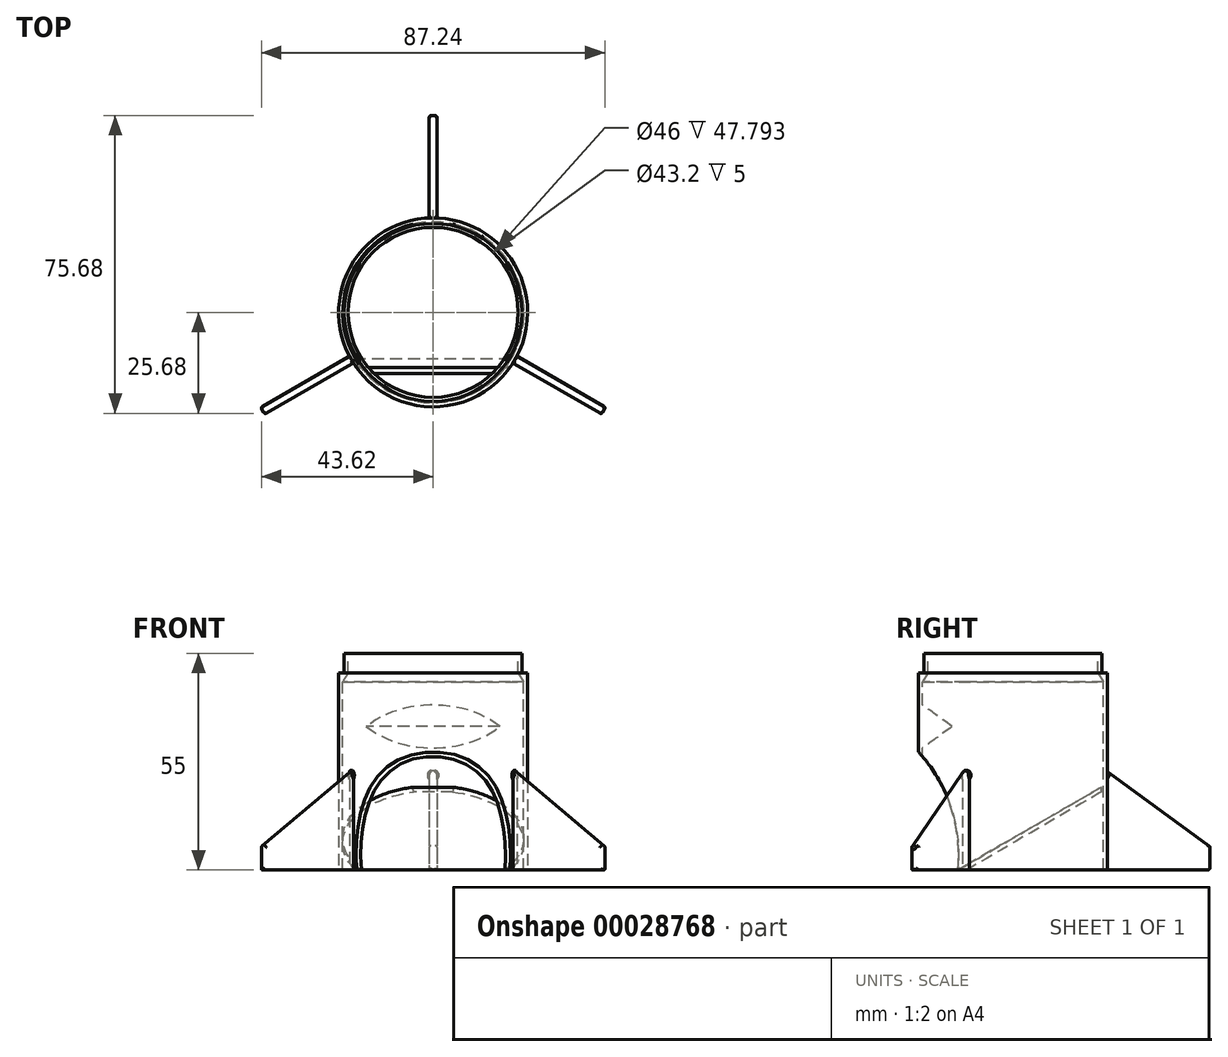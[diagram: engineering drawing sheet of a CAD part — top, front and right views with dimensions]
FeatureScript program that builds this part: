
annotation { "Feature Type Name" : "Feature", "Feature Type Description" : "" }
export const myFeature = defineFeature(function(context is Context, id is Id, definition is map)
    precondition{}
    {
        {
            var Q0;
            Q0=qCreatedBy(makeId("Top.planeOp"),FACE);
            var sketch = newSketch(context, id + "F0", { "sketchPlane" : qUnion([Q0])});
            skCircle(sketch, "E0", {"center": v(0, 0) * mm, "radius": 24 * mm});
            skSolve(sketch);
        }
        {
            var Q0;
            Q0=makeQuery(id+"F0.imprint","IMPRINT",FACE,{"disambiguationData":[TD([[makeQuery(id+"F0.imprint","IMPRINT",EDGE,{"derivedFrom":sQuery(id+"F0.wireOp",EDGE,"E0")}),1.0]])]});
            extrude(context, id + "F1", {"entities" : qUnion([Q0]), "depth" : 50 * mm});
        }
        {
            var Q0;
            Q0=makeQuery(id+"F1.opExtrude","CAP_FACE",FACE,{"disambiguationData":[OSD([sQuery(id+"F0.wireOp",EDGE,"E0")])],"isStart":false});
            var sketch = newSketch(context, id + "F2", { "sketchPlane" : qUnion([Q0])});
            skCircle(sketch, "E1", {"center": v(0, 0) * mm, "radius": 23 * mm});
            skSolve(sketch);
        }
        {
            var Q0;
            Q0=qSketchRegion(id+"F2",true);
            extrude(context, id + "F3", {"entities" : qUnion([Q0]), "operationType" : NewBodyOperationType.REMOVE, "endBound" : BoundingType.THROUGH_ALL, "oppositeDirection" : true, "depth" : 25 * mm});
        }
        {
            var Q0;
            Q0=qCreatedBy(makeId("Front.planeOp"),FACE);
            var sketch = newSketch(context, id + "F4", { "sketchPlane" : qUnion([Q0])});
            skLineSegment(sketch, "E2", {"start": v(0, 0) * mm, "end": v(0, 50) * mm});
            skLineSegment(sketch, "E3.0", {"start": v(-23.5, 50) * mm, "end": v(-23.5, 47) * mm});
            skLineSegment(sketch, "E4", {"start": v(-23.5, 50) * mm, "end": v(-22.6, 50) * mm});
            skLineSegment(sketch, "E5", {"start": v(-22.6, 50) * mm, "end": v(-22.6, 55) * mm});
            skLineSegment(sketch, "E6", {"start": v(-22.6, 55) * mm, "end": v(-21.6, 55) * mm});
            skLineSegment(sketch, "E7", {"start": v(-21.6, 55) * mm, "end": v(-21.6, 50) * mm});
            skLineSegment(sketch, "E8", {"start": v(-21.6, 50) * mm, "end": v(-23.5, 47) * mm});
            skLineSegment(sketch, "E9", {"start": v(-24, 50) * mm, "end": v(-23.5, 50) * mm});
            skSolve(sketch);
        }
        {
            var Q0;
            Q0=qSketchRegion(id+"F4",true);
            var Q1;
            Q1=makeQuery(id+"F3.boolean.opBoolean","COPY",FACE,{"derivedFrom":makeQuery(id+"F3.opExtrude","SWEPT_FACE",FACE,{"disambiguationData":[OSD([sQuery(id+"F2.wireOp",EDGE,"E1")])]})});
            revolve(context, id + "F5", {"operationType" : NewBodyOperationType.ADD, "entities" : qUnion([Q0]), "axis" : qUnion([Q1]), "revolveType" : RevolveType.FULL});
        }
        {
            var Q0;
            Q0=qCreatedBy(makeId("Top.planeOp"),FACE);
            var sketch = newSketch(context, id + "F6", { "sketchPlane" : qUnion([Q0])});
            skLineSegment(sketch, "E10", {"start": v(-1, 50) * mm, "end": v(-1, 23.5) * mm});
            skLineSegment(sketch, "E11", {"start": v(-1, 23.5) * mm, "end": v(1, 23.5) * mm});
            skLineSegment(sketch, "E12", {"start": v(1, 23.5) * mm, "end": v(1, 50) * mm});
            skLineSegment(sketch, "E13", {"start": v(-1, 50) * mm, "end": v(1, 50) * mm});
            skLineSegment(sketch, "E14.1.4", {"start": v(-20.85, -10.88) * mm, "end": v(-43.8, -24.13) * mm});
            skLineSegment(sketch, "E14.1.6", {"start": v(-42.8, -25.87) * mm, "end": v(-19.85, -12.62) * mm});
            skLineSegment(sketch, "E14.1.8", {"start": v(-19.85, -12.62) * mm, "end": v(-20.85, -10.88) * mm});
            skLineSegment(sketch, "E14.1.11", {"start": v(-42.8, -25.87) * mm, "end": v(-43.8, -24.13) * mm});
            skLineSegment(sketch, "E14.2.4", {"start": v(19.85, -12.62) * mm, "end": v(42.8, -25.87) * mm});
            skLineSegment(sketch, "E14.2.6", {"start": v(43.8, -24.13) * mm, "end": v(20.85, -10.88) * mm});
            skLineSegment(sketch, "E14.2.8", {"start": v(20.85, -10.88) * mm, "end": v(19.85, -12.62) * mm});
            skLineSegment(sketch, "E14.2.11", {"start": v(43.8, -24.13) * mm, "end": v(42.8, -25.87) * mm});
            skPoint(sketch, "E14.center", {"position": v(0, 0) * mm});
            skSolve(sketch);
        }
        {
            var Q0;
            Q0=qSketchRegion(id+"F6",true);
            extrude(context, id + "F7", {"entities" : qUnion([Q0]), "operationType" : NewBodyOperationType.ADD, "depth" : 25 * mm});
        }
        {
            var Q0;
            Q0=makeQuery(id+"F7.opExtrude","SWEPT_FACE",FACE,{"disambiguationData":[OSD([sQuery(id+"F6.wireOp",EDGE,"E14.1.6")])]});
            var sketch = newSketch(context, id + "F8", { "sketchPlane" : qUnion([Q0])});
            skLineSegment(sketch, "E15", {"start": v(-23.98, 25) * mm, "end": v(-50, 25) * mm});
            skLineSegment(sketch, "E16", {"start": v(-50, 25) * mm, "end": v(-50, 6) * mm});
            skLineSegment(sketch, "E17", {"start": v(-50, 6) * mm, "end": v(-23.98, 25) * mm});
            skSolve(sketch);
        }
        {
            var Q0;
            Q0=qSketchRegion(id+"F8",true);
            extrude(context, id + "F9", {"entities" : qUnion([Q0]), "operationType" : NewBodyOperationType.REMOVE, "oppositeDirection" : true, "depth" : 2 * mm});
        }
        {
            var Q0;
            Q0=makeQuery(id+"F7.opExtrude","SWEPT_FACE",FACE,{"disambiguationData":[OSD([sQuery(id+"F6.wireOp",EDGE,"E14.2.6")])]});
            var sketch = newSketch(context, id + "F10", { "sketchPlane" : qUnion([Q0])});
            skLineSegment(sketch, "E18", {"start": v(-23.98, 25) * mm, "end": v(-50, 25) * mm});
            skLineSegment(sketch, "E19", {"start": v(-50, 25) * mm, "end": v(-50, 6) * mm});
            skLineSegment(sketch, "E20", {"start": v(-50, 6) * mm, "end": v(-23.98, 25) * mm});
            skSolve(sketch);
        }
        {
            var Q0;
            Q0=qSketchRegion(id+"F10",true);
            extrude(context, id + "F11", {"entities" : qUnion([Q0]), "operationType" : NewBodyOperationType.REMOVE, "oppositeDirection" : true, "depth" : 2 * mm});
        }
        {
            var Q0;
            Q0=makeQuery(id+"F7.opExtrude","SWEPT_FACE",FACE,{"disambiguationData":[OSD([sQuery(id+"F6.wireOp",EDGE,"E10")])]});
            var sketch = newSketch(context, id + "F12", { "sketchPlane" : qUnion([Q0])});
            skLineSegment(sketch, "E21", {"start": v(-23.98, 25) * mm, "end": v(-50, 25) * mm});
            skLineSegment(sketch, "E22", {"start": v(-50, 25) * mm, "end": v(-50, 6) * mm});
            skLineSegment(sketch, "E23", {"start": v(-23.98, 25) * mm, "end": v(-50, 6) * mm});
            skSolve(sketch);
        }
        {
            var Q0;
            Q0=qSketchRegion(id+"F12",true);
            extrude(context, id + "F13", {"entities" : qUnion([Q0]), "operationType" : NewBodyOperationType.REMOVE, "oppositeDirection" : true, "depth" : 2 * mm});
        }
        {
            var Q0;
            Q0=makeQuery(id+"F13.boolean.opBoolean","COPY",FACE,{"derivedFrom":makeQuery(id+"F13.opExtrude","SWEPT_FACE",FACE,{"disambiguationData":[OSD([sQuery(id+"F12.wireOp",EDGE,"E23")])]})});
            var Q1;
            Q1=makeQuery(id+"F9.boolean.opBoolean","COPY",FACE,{"derivedFrom":makeQuery(id+"F9.opExtrude","SWEPT_FACE",FACE,{"disambiguationData":[OSD([sQuery(id+"F8.wireOp",EDGE,"E17")])]})});
            var Q2;
            Q2=makeQuery(id+"F11.boolean.opBoolean","COPY",FACE,{"derivedFrom":makeQuery(id+"F11.opExtrude","SWEPT_FACE",FACE,{"disambiguationData":[OSD([sQuery(id+"F10.wireOp",EDGE,"E20")])]})});
            fillet(context, id + "F14", {"entities" : qUnion([Q0, Q1, Q2]), "radius" : .5 * mm, "allowEdgeOverflow" : false});
        }
        {
            var Q0;
            Q0=makeQuery(id+"F7.opExtrude","SWEPT_FACE",FACE,{"disambiguationData":[OSD([sQuery(id+"F6.wireOp",EDGE,"E14.1.11")])]});
            var Q1;
            Q1=makeQuery(id+"F7.opExtrude","SWEPT_FACE",FACE,{"disambiguationData":[OSD([sQuery(id+"F6.wireOp",EDGE,"E14.2.11")])]});
            var Q2;
            Q2=makeQuery(id+"F7.opExtrude","SWEPT_FACE",FACE,{"disambiguationData":[OSD([sQuery(id+"F6.wireOp",EDGE,"E13")])]});
            fillet(context, id + "F15", {"entities" : qUnion([Q0, Q1, Q2]), "radius" : .5 * mm, "tangentPropagation" : true, "allowEdgeOverflow" : false});
        }
        {
            var Q0;
            Q0=qCreatedBy(makeId("Right.planeOp"),FACE);
            var sketch = newSketch(context, id + "F16", { "sketchPlane" : qUnion([Q0])});
            skLineSegment(sketch, "E24", {"start": v(-24, 0) * mm, "end": v(-24, 30) * mm});
            skArc(sketch, "E25", {"start": v(-14, 0) * mm, "mid": v(-15.84, 16.05) * mm, "end": v(-24, 30) * mm});
            skLineSegment(sketch, "E26", {"start": v(-24, 0) * mm, "end": v(-14, 0) * mm});
            skSolve(sketch);
        }
        {
            var Q0;
            Q0=qSketchRegion(id+"F16",true);
            extrude(context, id + "F17", {"entities" : qUnion([Q0]), "operationType" : NewBodyOperationType.REMOVE, "oppositeDirection" : true, "depth" : 20 * mm, "hasSecondDirection" : true, "secondDirectionOppositeDirection" : false, "secondDirectionDepth" : 20 * mm});
        }
        {
            var Q0;
            Q0=qCreatedBy(makeId("Right.planeOp"),FACE);
            var sketch = newSketch(context, id + "F18", { "sketchPlane" : qUnion([Q0])});
            skCircle(sketch, "E27", {"center": v(0, 27.55) * mm, "radius": 3 * mm});
            skLineSegment(sketch, "E28.rect.bottom", {"start": v(-3, 21.55) * mm, "end": v(3, 21.55) * mm});
            skLineSegment(sketch, "E28.rect.top", {"start": v(-3, 27.55) * mm, "end": v(3, 27.55) * mm});
            skLineSegment(sketch, "E28.rect.left", {"start": v(-3, 21.55) * mm, "end": v(-3, 27.55) * mm});
            skLineSegment(sketch, "E28.rect.right", {"start": v(3, 21.55) * mm, "end": v(3, 27.55) * mm});
            skPoint(sketch, "E28.rect.middle", {"position": v(0, 24.55) * mm});
            skSolve(sketch);
        }
        {
            var Q0;
            Q0=qCreatedBy(makeId("Right.planeOp"),FACE);
            var sketch = newSketch(context, id + "F19", { "sketchPlane" : qUnion([Q0])});
            skPoint(sketch, "E29.0", {"position": v(-14, 0) * mm});
            skLineSegment(sketch, "E30", {"start": v(-23, 30.97) * mm, "end": v(-15.49, 36.45) * mm});
            skLineSegment(sketch, "E31", {"start": v(-15.49, 36.45) * mm, "end": v(-23, 41.91) * mm});
            skLineSegment(sketch, "E32", {"start": v(-23, 41.91) * mm, "end": v(-23, 30.97) * mm});
            skLineSegment(sketch, "E33", {"start": v(22.42, 21.03) * mm, "end": v(-14, 0) * mm});
            skLineSegment(sketch, "E34", {"start": v(22.46, 19.84) * mm, "end": v(-11.9, 0) * mm});
            skLineSegment(sketch, "E35", {"start": v(-11.9, 0) * mm, "end": v(-14, 0) * mm});
            skLineSegment(sketch, "E36", {"start": v(22.42, 21.03) * mm, "end": v(22.46, 19.84) * mm});
            skSolve(sketch);
        }
        {
            var Q0;
            Q0=qSketchRegion(id+"F19",true);
            extrude(context, id + "F20", {"entities" : qUnion([Q0]), "operationType" : NewBodyOperationType.ADD, "endBound" : BoundingType.UP_TO_NEXT, "depth" : 25 * mm, "hasSecondDirection" : true, "secondDirectionBound" : SecondDirectionBoundingType.UP_TO_NEXT, "secondDirectionOppositeDirection" : true, "secondDirectionDepth" : 25 * mm});
        }
    });
